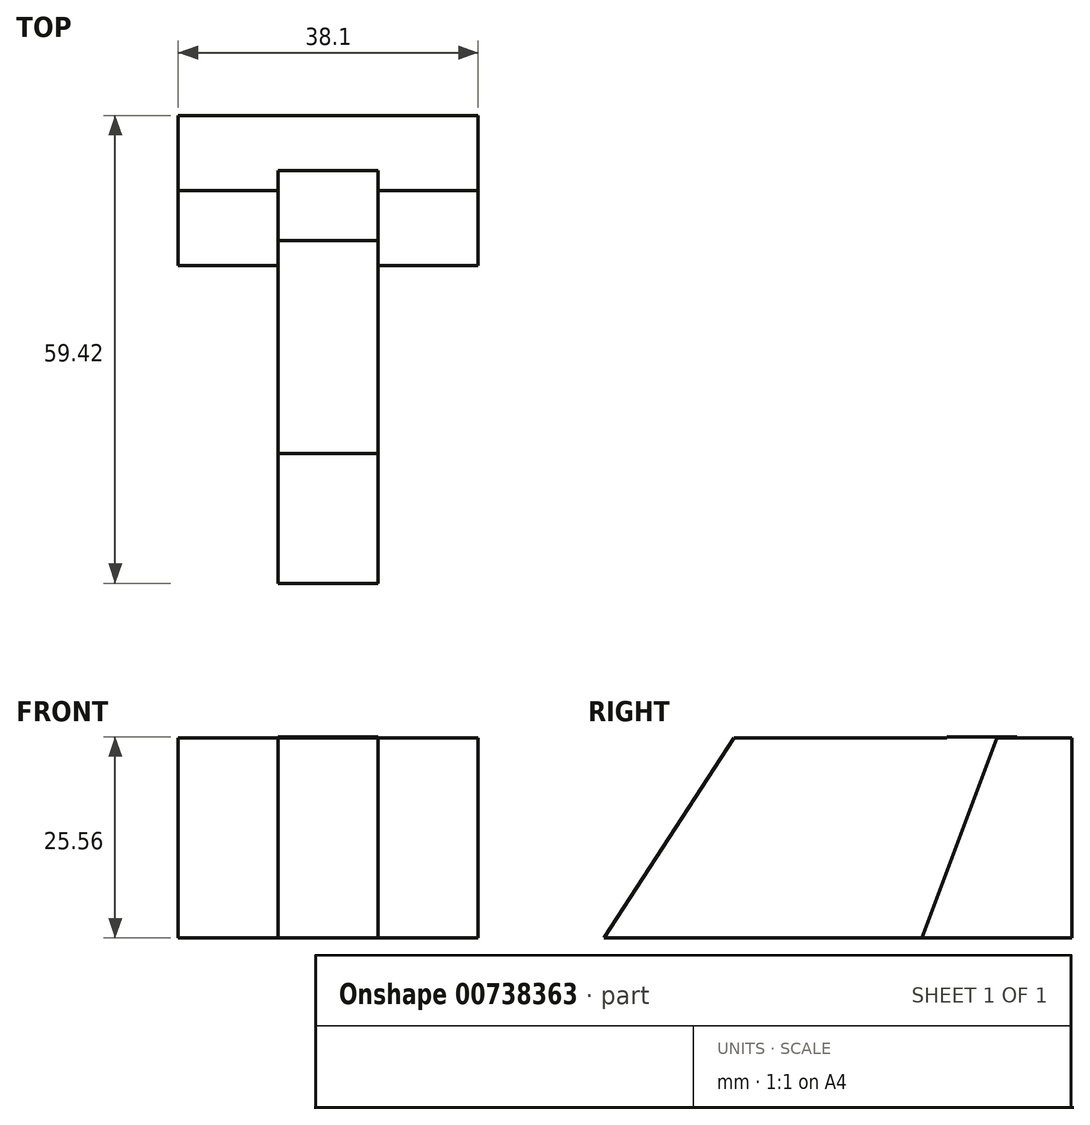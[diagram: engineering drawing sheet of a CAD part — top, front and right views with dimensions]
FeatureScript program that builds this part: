
annotation { "Feature Type Name" : "Feature", "Feature Type Description" : "" }
export const myFeature = defineFeature(function(context is Context, id is Id, definition is map)
    precondition{}
    {
        {
            var Q0;
            Q0=qCreatedBy(makeId("Top.planeOp"),FACE);
            var sketch = newSketch(context, id + "F0", { "sketchPlane" : qUnion([Q0])});
            skLineSegment(sketch, "E0", {"start": v(0, 0) * mm, "end": v(0, 40.37) * mm});
            skLineSegment(sketch, "E1", {"start": v(0, 40.37) * mm, "end": v(-12.7, 40.37) * mm});
            skLineSegment(sketch, "E2", {"start": v(-12.7, 40.37) * mm, "end": v(-12.7, 59.42) * mm});
            skLineSegment(sketch, "E3", {"start": v(-12.7, 59.42) * mm, "end": v(25.4, 59.42) * mm});
            skLineSegment(sketch, "E4", {"start": v(25.4, 59.42) * mm, "end": v(25.4, 40.37) * mm});
            skLineSegment(sketch, "E5", {"start": v(25.4, 40.37) * mm, "end": v(12.7, 40.37) * mm});
            skLineSegment(sketch, "E6", {"start": v(12.7, 40.37) * mm, "end": v(12.7, 0) * mm});
            skLineSegment(sketch, "E7", {"start": v(12.7, 0) * mm, "end": v(0, 0) * mm});
            skSolve(sketch);
        }
        {
            var Q0;
            Q0=makeQuery(id+"F0.imprint","IMPRINT",FACE,{"disambiguationData":[TD([[makeQuery(id+"F0.imprint","IMPRINT",EDGE,{"derivedFrom":sQuery(id+"F0.wireOp",EDGE,"E0")}),-1.0]])]});
            extrude(context, id + "F1", {"entities" : qUnion([Q0]), "depth" : 25.4 * mm, "offsetDistance" : 25.4 * mm});
        }
        {
            var Q0;
            Q0=qCreatedBy(makeId("Right.planeOp"),FACE);
            var sketch = newSketch(context, id + "F2", { "sketchPlane" : qUnion([Q0])});
            skLineSegment(sketch, "E8", {"start": v(0, 0) * mm, "end": v(8.63, 25.5) * mm});
            skLineSegment(sketch, "E9", {"start": v(8.63, 25.5) * mm, "end": v(21.36, 25.5) * mm});
            skLineSegment(sketch, "E10", {"start": v(21.36, 25.5) * mm, "end": v(13.84, 0) * mm});
            skLineSegment(sketch, "E11", {"start": v(13.84, 0) * mm, "end": v(0, 0) * mm});
            skSolve(sketch);
        }
        {
            var Q0;
            Q0=makeQuery(id+"F2.imprint","IMPRINT",FACE,{"disambiguationData":[TD([[makeQuery(id+"F2.imprint","IMPRINT",EDGE,{"derivedFrom":sQuery(id+"F2.wireOp",EDGE,"E8")}),-1.0]])]});
            var Q1;
            Q1=makeQuery(id+"F1.opExtrude","SWEPT_FACE",FACE,{"disambiguationData":[OSD([sQuery(id+"F0.wireOp",EDGE,"E0")])]});
            extrude(context, id + "F3", {"entities" : qUnion([Q0, Q1]), "operationType" : NewBodyOperationType.REMOVE, "oppositeDirection" : true, "depth" : 12.7 * mm, "offsetDistance" : 25.4 * mm});
        }
        {
            var Q0;
            Q0=makeQuery(id+"F1.opExtrude","SWEPT_FACE",FACE,{"disambiguationData":[OSD([sQuery(id+"F0.wireOp",EDGE,"E6")])]});
            var sketch = newSketch(context, id + "F4", { "sketchPlane" : qUnion([Q0])});
            skLineSegment(sketch, "E12", {"start": v(16.46, 25.4) * mm, "end": v(0, 0) * mm});
            skSolve(sketch);
        }
        {
            var Q0;
            {var subQ0=sQuery(id+"F4.wireOp",EDGE,"E12");Q0=makeQuery(id+"F4.imprint","IMPRINT",FACE,{"disambiguationData":[TD([[makeQuery(id+"F4.imprint","IMPRINT",EDGE,{"derivedFrom":subQ0}),-1.0]])]});}
            extrude(context, id + "F5", {"entities" : qUnion([Q0]), "operationType" : NewBodyOperationType.REMOVE, "oppositeDirection" : true, "depth" : 25.4 * mm, "offsetDistance" : 25.4 * mm});
        }
        {
            var Q0;
            Q0=makeQuery(id+"F1.opExtrude","SWEPT_FACE",FACE,{"disambiguationData":[OSD([sQuery(id+"F0.wireOp",EDGE,"E2")])]});
            var sketch = newSketch(context, id + "F6", { "sketchPlane" : qUnion([Q0])});
            skLineSegment(sketch, "E13", {"start": v(-49.9, 25.4) * mm, "end": v(-40.37, 0) * mm});
            skSolve(sketch);
        }
        {
            var Q0;
            Q0 = qSketchRegion(id + "F6", true);
            var Q1;
            {var subQ0=sQuery(id+"F6.wireOp",EDGE,"E13");Q1=makeQuery(id+"F6.imprint","IMPRINT",FACE,{"disambiguationData":[TD([[makeQuery(id+"F6.imprint","IMPRINT",EDGE,{"derivedFrom":subQ0}),1.0]])]});}
            extrude(context, id + "F7", {"entities" : qUnion([Q0, Q1]), "operationType" : NewBodyOperationType.REMOVE, "oppositeDirection" : true, "depth" : 12.7 * mm, "offsetDistance" : 25.4 * mm});
        }
        {
            var Q0;
            Q0=qCreatedBy(makeId("Right.planeOp"),FACE);
            var sketch = newSketch(context, id + "F8", { "sketchPlane" : qUnion([Q0])});
            skLineSegment(sketch, "E14", {"start": v(43.6, 0) * mm, "end": v(52.44, 25.56) * mm});
            skLineSegment(sketch, "E15", {"start": v(52.44, 25.56) * mm, "end": v(43.54, 25.56) * mm});
            skLineSegment(sketch, "E16", {"start": v(43.54, 25.56) * mm, "end": v(43.6, 0) * mm});
            skSolve(sketch);
        }
        {
            var Q0;
            Q0 = qSketchRegion(id + "F8", true);
            extrude(context, id + "F9", {"entities" : qUnion([Q0]), "operationType" : NewBodyOperationType.ADD, "depth" : 12.7 * mm, "offsetDistance" : 25.4 * mm});
        }
        {
            var Q0;
            Q0=makeQuery(id+"F1.opExtrude","SWEPT_FACE",FACE,{"disambiguationData":[OSD([sQuery(id+"F0.wireOp",EDGE,"E4")])]});
            var sketch = newSketch(context, id + "F10", { "sketchPlane" : qUnion([Q0])});
            skLineSegment(sketch, "E17", {"start": v(40.37, 0) * mm, "end": v(49.9, 25.4) * mm});
            skSolve(sketch);
        }
        {
            var Q0;
            Q0 = qSketchRegion(id + "F10", true);
            var Q1;
            {var subQ0=sQuery(id+"F10.wireOp",EDGE,"E17");Q1=makeQuery(id+"F10.imprint","IMPRINT",FACE,{"disambiguationData":[TD([[makeQuery(id+"F10.imprint","IMPRINT",EDGE,{"derivedFrom":subQ0}),1.0]])]});}
            extrude(context, id + "F11", {"entities" : qUnion([Q0, Q1]), "operationType" : NewBodyOperationType.REMOVE, "oppositeDirection" : true, "depth" : 12.7 * mm, "offsetDistance" : 25.4 * mm});
        }
    });
